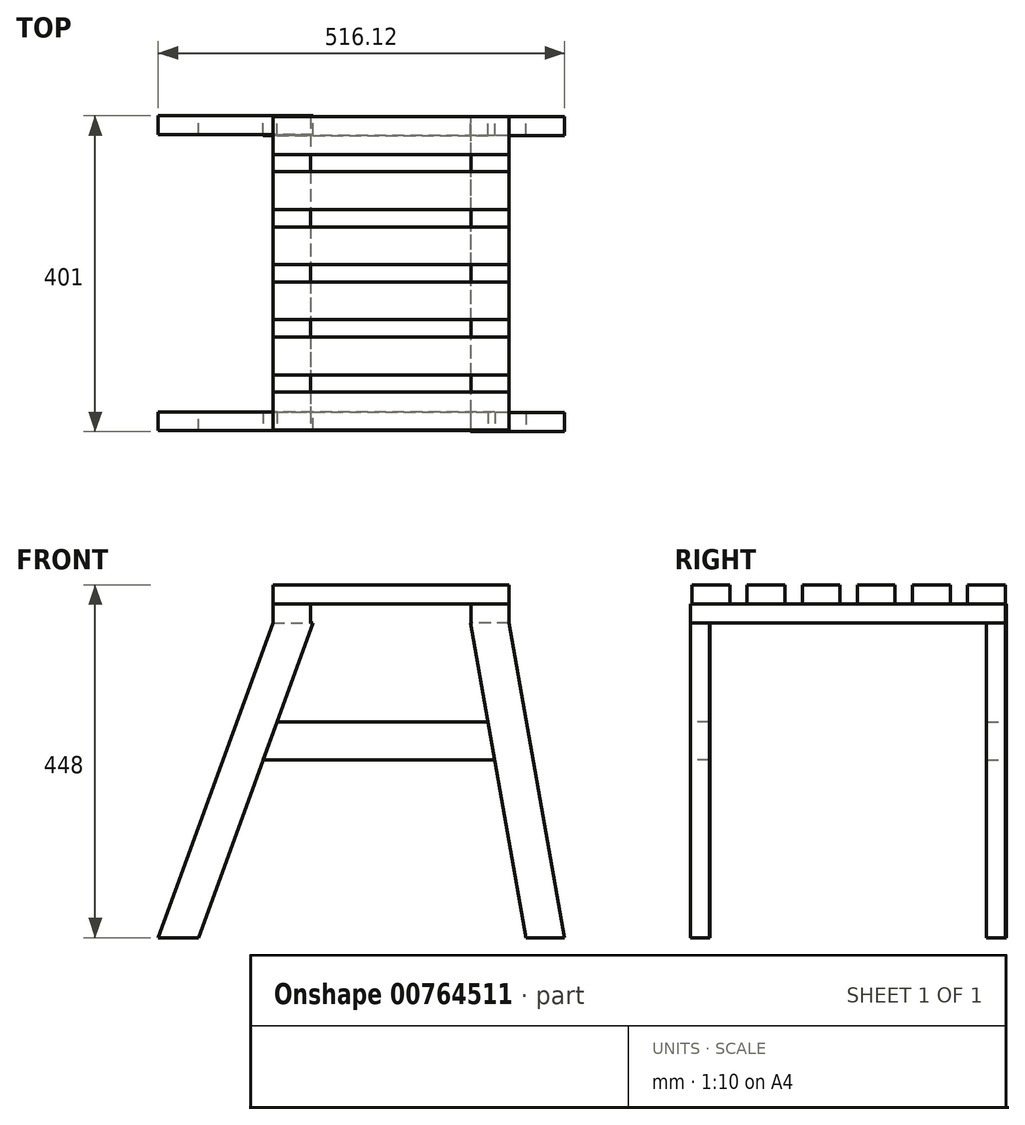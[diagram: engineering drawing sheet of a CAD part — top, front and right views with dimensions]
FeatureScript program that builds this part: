
annotation { "Feature Type Name" : "Feature", "Feature Type Description" : "" }
export const myFeature = defineFeature(function(context is Context, id is Id, definition is map)
    precondition{}
    {
        {
            var Q0;
            Q0=qCreatedBy(makeId("Front.planeOp"),FACE);
            var sketch = newSketch(context, id + "F0", { "sketchPlane" : qUnion([Q0])});
            skLineSegment(sketch, "E0", {"start": v(0, 0) * mm, "end": v(51.08, 0) * mm});
            skLineSegment(sketch, "E1", {"start": v(0, 0) * mm, "end": v(145.59, 400) * mm});
            skLineSegment(sketch, "E2", {"start": v(145.59, 400) * mm, "end": v(196.67, 400) * mm});
            skLineSegment(sketch, "E3", {"start": v(196.67, 400) * mm, "end": v(51.08, 0) * mm});
            skSolve(sketch);
        }
        {
            var Q0;
            Q0=makeQuery(id+"F0.imprint","IMPRINT",FACE,{"disambiguationData":[TD([[makeQuery(id+"F0.imprint","IMPRINT",EDGE,{"derivedFrom":sQuery(id+"F0.wireOp",EDGE,"E0")}),1.0]])]});
            extrude(context, id + "F1", {"entities" : qUnion([Q0]), "depth" : 24 * mm, "offsetDistance" : 25 * mm});
        }
        {
            var Q0;
            Q0=makeQuery(id+"F1.opExtrude","CAP_FACE",FACE,{"disambiguationData":[OSD([sQuery(id+"F0.wireOp",EDGE,"E0"),sQuery(id+"F0.wireOp",EDGE,"E1"),sQuery(id+"F0.wireOp",EDGE,"E2"),sQuery(id+"F0.wireOp",EDGE,"E3")])],"isStart":false});
            var sketch = newSketch(context, id + "F2", { "sketchPlane" : qUnion([Q0])});
            skLineSegment(sketch, "E4.bottom", {"start": v(145.59, 400) * mm, "end": v(193.59, 400) * mm});
            skLineSegment(sketch, "E4.top", {"start": v(145.59, 424) * mm, "end": v(193.59, 424) * mm});
            skLineSegment(sketch, "E4.left", {"start": v(145.59, 400) * mm, "end": v(145.59, 424) * mm});
            skLineSegment(sketch, "E4.right", {"start": v(193.59, 400) * mm, "end": v(193.59, 424) * mm});
            skSolve(sketch);
        }
        {
            var Q0;
            Q0 = qSketchRegion(id + "F2", true);
            extrude(context, id + "F3", {"entities" : qUnion([Q0]), "operationType" : NewBodyOperationType.ADD, "oppositeDirection" : true, "depth" : 400 * mm, "offsetDistance" : 25 * mm});
        }
        {
            var Q0;
            Q0=makeQuery(id+"F3.opExtrude","CAP_FACE",FACE,{"disambiguationData":[OSD([sQuery(id+"F2.wireOp",EDGE,"E4.bottom"),sQuery(id+"F2.wireOp",EDGE,"E4.top"),sQuery(id+"F2.wireOp",EDGE,"E4.left"),sQuery(id+"F2.wireOp",EDGE,"E4.right")])],"isStart":false});
            var sketch = newSketch(context, id + "F4", { "sketchPlane" : qUnion([Q0])});
            skLineSegment(sketch, "E5", {"start": v(0, 0) * mm, "end": v(-145.59, 400) * mm});
            skLineSegment(sketch, "E6", {"start": v(-145.59, 400) * mm, "end": v(-196.67, 400) * mm});
            skLineSegment(sketch, "E7", {"start": v(-196.67, 400) * mm, "end": v(-51.08, 0) * mm});
            skLineSegment(sketch, "E8", {"start": v(-51.08, 0) * mm, "end": v(0, 0) * mm});
            skSolve(sketch);
        }
        {
            var Q0;
            Q0 = qSketchRegion(id + "F4", true);
            extrude(context, id + "F5", {"entities" : qUnion([Q0]), "operationType" : NewBodyOperationType.ADD, "oppositeDirection" : true, "depth" : 24 * mm, "offsetDistance" : 25 * mm});
        }
        {
            var Q0;
            Q0=makeQuery(id+"F3.opExtrude","SWEPT_FACE",FACE,{"disambiguationData":[OSD([sQuery(id+"F2.wireOp",EDGE,"E4.left")])]});
            var sketch = newSketch(context, id + "F6", { "sketchPlane" : qUnion([Q0])});
            skLineSegment(sketch, "E9.bottom", {"start": v(-375, 424) * mm, "end": v(-327, 424) * mm});
            skLineSegment(sketch, "E9.top", {"start": v(-375, 448) * mm, "end": v(-327, 448) * mm});
            skLineSegment(sketch, "E9.left", {"start": v(-375, 424) * mm, "end": v(-375, 448) * mm});
            skLineSegment(sketch, "E9.right", {"start": v(-327, 424) * mm, "end": v(-327, 448) * mm});
            skLineSegment(sketch, "E10.bottom", {"start": v(-305, 424) * mm, "end": v(-257, 424) * mm});
            skLineSegment(sketch, "E10.top", {"start": v(-305, 448) * mm, "end": v(-257, 448) * mm});
            skLineSegment(sketch, "E10.left", {"start": v(-305, 424) * mm, "end": v(-305, 448) * mm});
            skLineSegment(sketch, "E10.right", {"start": v(-257, 424) * mm, "end": v(-257, 448) * mm});
            skLineSegment(sketch, "E11.bottom", {"start": v(-235, 424) * mm, "end": v(-187, 424) * mm});
            skLineSegment(sketch, "E11.top", {"start": v(-235, 448) * mm, "end": v(-187, 448) * mm});
            skLineSegment(sketch, "E11.left", {"start": v(-235, 424) * mm, "end": v(-235, 448) * mm});
            skLineSegment(sketch, "E11.right", {"start": v(-187, 424) * mm, "end": v(-187, 448) * mm});
            skLineSegment(sketch, "E12.bottom", {"start": v(-165, 424) * mm, "end": v(-117, 424) * mm});
            skLineSegment(sketch, "E12.top", {"start": v(-165, 448) * mm, "end": v(-117, 448) * mm});
            skLineSegment(sketch, "E12.left", {"start": v(-165, 424) * mm, "end": v(-165, 448) * mm});
            skLineSegment(sketch, "E12.right", {"start": v(-117, 424) * mm, "end": v(-117, 448) * mm});
            skLineSegment(sketch, "E13.bottom", {"start": v(-95, 424) * mm, "end": v(-47, 424) * mm});
            skLineSegment(sketch, "E13.top", {"start": v(-95, 448) * mm, "end": v(-47, 448) * mm});
            skLineSegment(sketch, "E13.left", {"start": v(-95, 424) * mm, "end": v(-95, 448) * mm});
            skLineSegment(sketch, "E13.right", {"start": v(-47, 424) * mm, "end": v(-47, 448) * mm});
            skLineSegment(sketch, "E14.bottom", {"start": v(-25, 424) * mm, "end": v(23, 424) * mm});
            skLineSegment(sketch, "E14.top", {"start": v(-25, 448) * mm, "end": v(23, 448) * mm});
            skLineSegment(sketch, "E14.left", {"start": v(-25, 424) * mm, "end": v(-25, 448) * mm});
            skLineSegment(sketch, "E14.right", {"start": v(23, 424) * mm, "end": v(23, 448) * mm});
            skSolve(sketch);
        }
        {
            var Q0;
            Q0 = qSketchRegion(id + "F6", true);
            extrude(context, id + "F7", {"entities" : qUnion([Q0]), "oppositeDirection" : true, "depth" : 300 * mm, "offsetDistance" : 25 * mm});
        }
        {
            var Q0;
            Q0=makeQuery(id+"F7.opExtrude","SWEPT_FACE",FACE,{"disambiguationData":[OSD([sQuery(id+"F6.wireOp",EDGE,"E9.left")])]});
            var sketch = newSketch(context, id + "F8", { "sketchPlane" : qUnion([Q0])});
            skLineSegment(sketch, "E15.bottom", {"start": v(-445.59, 424) * mm, "end": v(-397.59, 424) * mm});
            skLineSegment(sketch, "E15.top", {"start": v(-445.59, 400) * mm, "end": v(-397.59, 400) * mm});
            skLineSegment(sketch, "E15.left", {"start": v(-445.59, 424) * mm, "end": v(-445.59, 400) * mm});
            skLineSegment(sketch, "E15.right", {"start": v(-397.59, 424) * mm, "end": v(-397.59, 400) * mm});
            skSolve(sketch);
        }
        {
            var Q0;
            Q0 = qSketchRegion(id + "F8", true);
            extrude(context, id + "F9", {"entities" : qUnion([Q0]), "oppositeDirection" : true, "depth" : 400 * mm, "offsetDistance" : 25 * mm});
        }
        {
            var Q0;
            Q0=makeQuery(id+"F9.opExtrude","CAP_FACE",FACE,{"disambiguationData":[OSD([sQuery(id+"F8.wireOp",EDGE,"E15.bottom"),sQuery(id+"F8.wireOp",EDGE,"E15.top"),sQuery(id+"F8.wireOp",EDGE,"E15.left"),sQuery(id+"F8.wireOp",EDGE,"E15.right")])],"isStart":true});
            var sketch = newSketch(context, id + "F10", { "sketchPlane" : qUnion([Q0])});
            skLineSegment(sketch, "E16", {"start": v(-445.59, 400) * mm, "end": v(-516.12, 0) * mm});
            skLineSegment(sketch, "E17", {"start": v(-516.12, 0) * mm, "end": v(-467.38, 0) * mm});
            skLineSegment(sketch, "E18", {"start": v(-467.38, 0) * mm, "end": v(-396.85, 400) * mm});
            skLineSegment(sketch, "E19", {"start": v(-396.85, 400) * mm, "end": v(-445.59, 400) * mm});
            skSolve(sketch);
        }
        {
            var Q0;
            Q0 = qSketchRegion(id + "F10", true);
            extrude(context, id + "F11", {"entities" : qUnion([Q0]), "oppositeDirection" : true, "depth" : 24 * mm, "offsetDistance" : 25 * mm});
        }
        {
            var Q0;
            Q0=makeQuery(id+"F9.opExtrude","CAP_FACE",FACE,{"disambiguationData":[OSD([sQuery(id+"F8.wireOp",EDGE,"E15.bottom"),sQuery(id+"F8.wireOp",EDGE,"E15.top"),sQuery(id+"F8.wireOp",EDGE,"E15.left"),sQuery(id+"F8.wireOp",EDGE,"E15.right")])],"isStart":false});
            var sketch = newSketch(context, id + "F12", { "sketchPlane" : qUnion([Q0])});
            skLineSegment(sketch, "E20", {"start": v(445.59, 400) * mm, "end": v(516.12, 0) * mm});
            skLineSegment(sketch, "E21", {"start": v(516.12, 0) * mm, "end": v(467.38, 0) * mm});
            skLineSegment(sketch, "E22", {"start": v(467.38, 0) * mm, "end": v(396.85, 400) * mm});
            skLineSegment(sketch, "E23", {"start": v(396.85, 400) * mm, "end": v(445.59, 400) * mm});
            skSolve(sketch);
        }
        {
            var Q0;
            Q0 = qSketchRegion(id + "F12", true);
            extrude(context, id + "F13", {"entities" : qUnion([Q0]), "operationType" : NewBodyOperationType.ADD, "oppositeDirection" : true, "depth" : 24 * mm, "offsetDistance" : 25 * mm});
        }
        {
            var Q0;
            Q0=makeQuery(id+"F3.boolean.opBoolean","MERGE",FACE,{"derivedFrom":[makeQuery(id+"F1.opExtrude","CAP_FACE",FACE,{"disambiguationData":[OSD([sQuery(id+"F0.wireOp",EDGE,"E0"),sQuery(id+"F0.wireOp",EDGE,"E1"),sQuery(id+"F0.wireOp",EDGE,"E2"),sQuery(id+"F0.wireOp",EDGE,"E3")])],"isStart":false}),makeQuery(id+"F3.opExtrude","CAP_FACE",FACE,{"disambiguationData":[OSD([sQuery(id+"F2.wireOp",EDGE,"E4.bottom"),sQuery(id+"F2.wireOp",EDGE,"E4.top"),sQuery(id+"F2.wireOp",EDGE,"E4.left"),sQuery(id+"F2.wireOp",EDGE,"E4.right")])],"isStart":true})]});
            var sketch = newSketch(context, id + "F14", { "sketchPlane" : qUnion([Q0])});
            skLineSegment(sketch, "E24.0", {"start": v(467.38, 0) * mm, "end": v(396.85, 400) * mm});
            skLineSegment(sketch, "E24.1", {"start": v(196.67, 400) * mm, "end": v(51.08, 0) * mm});
            skLineSegment(sketch, "E25", {"start": v(150.8, 274) * mm, "end": v(419.06, 274) * mm});
            skLineSegment(sketch, "E26", {"start": v(419.06, 274) * mm, "end": v(427.53, 226) * mm});
            skLineSegment(sketch, "E27", {"start": v(427.53, 226) * mm, "end": v(133.34, 226) * mm});
            skLineSegment(sketch, "E28", {"start": v(133.34, 226) * mm, "end": v(150.8, 274) * mm});
            skSolve(sketch);
        }
        {
            var Q0;
            Q0 = qSketchRegion(id + "F14", true);
            extrude(context, id + "F15", {"entities" : qUnion([Q0]), "oppositeDirection" : true, "depth" : 24 * mm, "offsetDistance" : 25 * mm});
        }
        {
            var Q0;
            Q0=makeQuery(id+"F11.opExtrude","CAP_FACE",FACE,{"disambiguationData":[OSD([sQuery(id+"F10.wireOp",EDGE,"E16"),sQuery(id+"F10.wireOp",EDGE,"E17"),sQuery(id+"F10.wireOp",EDGE,"E18"),sQuery(id+"F10.wireOp",EDGE,"E19")])],"isStart":true});
            var sketch = newSketch(context, id + "F16", { "sketchPlane" : qUnion([Q0])});
            skLineSegment(sketch, "E29.0", {"start": v(-196.67, 400) * mm, "end": v(-51.08, 0) * mm});
            skLineSegment(sketch, "E29.1", {"start": v(-467.38, 0) * mm, "end": v(-396.85, 400) * mm});
            skLineSegment(sketch, "E30.0", {"start": v(-150.8, 274) * mm, "end": v(-419.06, 274) * mm});
            skLineSegment(sketch, "E31", {"start": v(-419.06, 274) * mm, "end": v(-150.8, 274) * mm, "construction": true});
            skLineSegment(sketch, "E32", {"start": v(-150.8, 274) * mm, "end": v(-133.34, 226) * mm, "construction": true});
            skLineSegment(sketch, "E33", {"start": v(-133.34, 226) * mm, "end": v(-427.53, 226) * mm, "construction": true});
            skLineSegment(sketch, "E34", {"start": v(-427.53, 226) * mm, "end": v(-419.06, 274) * mm, "construction": true});
            skLineSegment(sketch, "E35", {"start": v(-427.53, 226) * mm, "end": v(-133.34, 226) * mm});
            skLineSegment(sketch, "E36", {"start": v(-150.8, 274) * mm, "end": v(-133.34, 226) * mm});
            skSolve(sketch);
        }
        {
            var Q0;
            Q0 = qSketchRegion(id + "F16", true);
            extrude(context, id + "F17", {"entities" : qUnion([Q0]), "oppositeDirection" : true, "depth" : 24 * mm, "offsetDistance" : 25 * mm});
        }
    });
